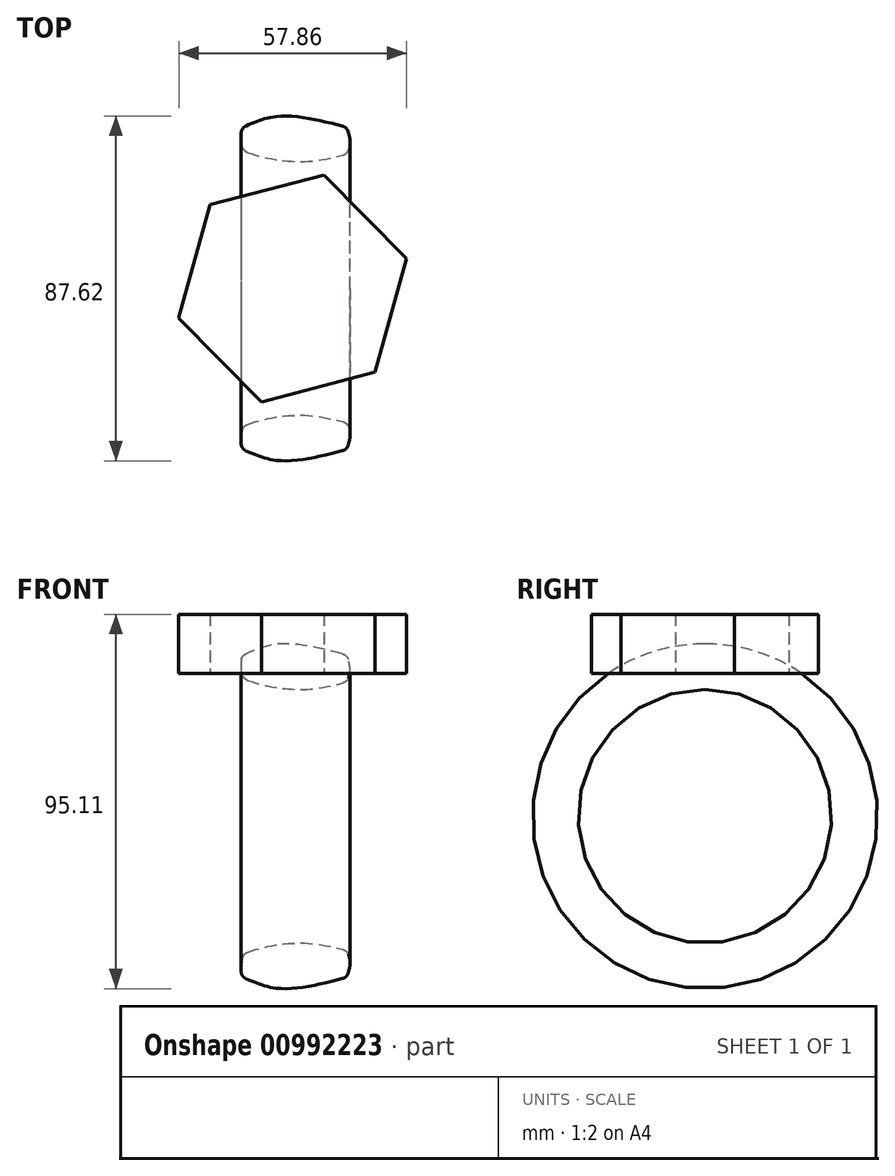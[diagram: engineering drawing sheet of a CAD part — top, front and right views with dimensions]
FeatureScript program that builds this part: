
annotation { "Feature Type Name" : "Feature", "Feature Type Description" : "" }
export const myFeature = defineFeature(function(context is Context, id is Id, definition is map)
    precondition{}
    {
        {
            var Q0;
            Q0=qCreatedBy(makeId("Front.planeOp"),FACE);
            var sketch = newSketch(context, id + "F0", { "sketchPlane" : qUnion([Q0])});
            skFitSpline(sketch, "E0", {"points": [v(-12.1, 34.78) * mm, v(0, 32.28) * mm, v(13.74, 34.13) * mm], "startDerivative": vector(24.43, -9.62) * mm, "endDerivative": vector(38.23, 9.9) * mm});
            skFitSpline(sketch, "E1", {"points": [v(13.74, 34.13) * mm, v(14.58, 36.94) * mm, v(13.74, 40.97) * mm], "startDerivative": vector(2.62, 5.84) * mm, "endDerivative": vector(-2.47, 7.78) * mm});
            skFitSpline(sketch, "E2", {"points": [v(13.74, 40.97) * mm, v(-3.11, 43.77) * mm, v(-12.57, 40.97) * mm], "startDerivative": vector(-31.87, 8.2) * mm, "endDerivative": vector(-20.23, -8.98) * mm});
            skFitSpline(sketch, "E3", {"points": [v(-12.57, 40.97) * mm, v(-13.13, 37.7) * mm, v(-12.1, 34.78) * mm], "startDerivative": vector(-3.65, -5.81) * mm, "endDerivative": vector(4.09, -5.03) * mm});
            skLineSegment(sketch, "E4", {"start": v(0, 0) * mm, "end": v(31.63, 0) * mm, "construction": true});
            skSolve(sketch);
        }
        {
            var Q0;
            Q0=makeQuery(id+"F0.imprint","IMPRINT",FACE,{"disambiguationData":[TD([[makeQuery(id+"F0.imprint","IMPRINT",EDGE,{"derivedFrom":sQuery(id+"F0.wireOp",EDGE,"E0")}),1.0]])]});
            var Q1;
            Q1=sQuery(id+"F0.wireOp",EDGE,"E4");
            revolve(context, id + "F1", {"surfaceOperationType" : NewSurfaceOperationType.NEW, "entities" : qUnion([Q0]), "axis" : qUnion([Q1]), "revolveType" : RevolveType.FULL});
        }
        {
            var Q0;
            Q0=makeQuery(id+"F1.opRevolve","SWEPT_EDGE",EDGE,{"disambiguationData":[OSD([sQuery(id+"F0.wireOp",EDGE,"E1"),sQuery(id+"F0.wireOp",EDGE,"E2")])]});
            var Q1;
            Q1=makeQuery(id+"F1.opRevolve","SWEPT_EDGE",EDGE,{"disambiguationData":[OSD([sQuery(id+"F0.wireOp",EDGE,"E0"),sQuery(id+"F0.wireOp",EDGE,"E1")])]});
            var Q2;
            Q2=makeQuery(id+"F1.opRevolve","SWEPT_EDGE",EDGE,{"disambiguationData":[OSD([sQuery(id+"F0.wireOp",EDGE,"E2"),sQuery(id+"F0.wireOp",EDGE,"E3")])]});
            var Q3;
            Q3=makeQuery(id+"F1.opRevolve","SWEPT_EDGE",EDGE,{"disambiguationData":[OSD([sQuery(id+"F0.wireOp",EDGE,"E0"),sQuery(id+"F0.wireOp",EDGE,"E3")])]});
            fillet(context, id + "F2", {"entities" : qUnion([Q0, Q1, Q2, Q3]), "radius" : 2 * mm, "tangentPropagation" : true, "allowEdgeOverflow" : false});
        }
        {
            var Q0;
            Q0=qCreatedBy(makeId("Top.planeOp"),FACE);
            var sketch = newSketch(context, id + "F3", { "sketchPlane" : qUnion([Q0])});
            skCircle(sketch, "E5.cCircle", {"center": v(0, 0) * mm, "radius": 25.89 * mm, "construction": true});
            skLineSegment(sketch, "E5.0", {"start": v(7.96, 28.82) * mm, "end": v(28.93, 7.52) * mm});
            skLineSegment(sketch, "E5.1", {"start": v(28.93, 7.52) * mm, "end": v(20.98, -21.3) * mm});
            skLineSegment(sketch, "E5.2", {"start": v(20.98, -21.3) * mm, "end": v(-7.96, -28.82) * mm});
            skLineSegment(sketch, "E5.3", {"start": v(-7.96, -28.82) * mm, "end": v(-28.93, -7.52) * mm});
            skLineSegment(sketch, "E5.4", {"start": v(-28.93, -7.52) * mm, "end": v(-20.98, 21.3) * mm});
            skLineSegment(sketch, "E5.5", {"start": v(-20.98, 21.3) * mm, "end": v(7.96, 28.82) * mm});
            skPoint(sketch, "E5.0.midPoint", {"position": v(18.45, 18.17) * mm});
            skSolve(sketch);
        }
        {
            var Q0;
            Q0 = qSketchRegion(id + "F3", true);
            extrude(context, id + "F4", {"entities" : qUnion([Q0]), "depth" : 15 * mm, "offsetDistance" : 25 * mm});
        }
        {
            var Q0;
            Q0=makeQuery(id+"F4.opExtrude","SWEPT_BODY",BODY,{"disambiguationData":[OSD([sQuery(id+"F3.wireOp",EDGE,"E5.0"),sQuery(id+"F3.wireOp",EDGE,"E5.1"),sQuery(id+"F3.wireOp",EDGE,"E5.2"),sQuery(id+"F3.wireOp",EDGE,"E5.3"),sQuery(id+"F3.wireOp",EDGE,"E5.4"),sQuery(id+"F3.wireOp",EDGE,"E5.5")])]});
            transform(context, id + "F5", {"entities" : qUnion([Q0]), "transformType" : TransformType.TRANSLATION_3D, "dx" : 0 * mm, "dy" : 0 * mm, "dz" : 36.3 * mm, "makeCopy" : false});
        }
    });
